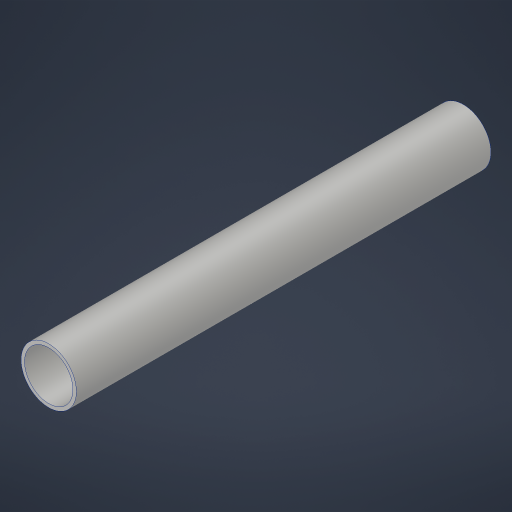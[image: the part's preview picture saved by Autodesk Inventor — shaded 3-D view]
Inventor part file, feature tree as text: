
AUTODESK INVENTOR PART (.ipt)
format: ipt  version: 2023.4 (Build 274418000, 418)  size: 172,032 bytes
history: native  units: in
note: dims shown in document units (in); Inventor stores cm internally (conversion verified against a paired STEP export)
features: extrude x1, sketch x1
ambient origin geometry x8: Origin, YZ Plane, XZ Plane, XY Plane, X Axis, Y Axis, Z Axis, Center Point
bodies: Solid1 (feature_tree)
feature tree (2):
  extrude  "Extrusion1"  Depth=15.0in
  sketch  "Sketch1"  dims[d0=2.0in d1=0.125in d2=15.0in d3=0.0in]
